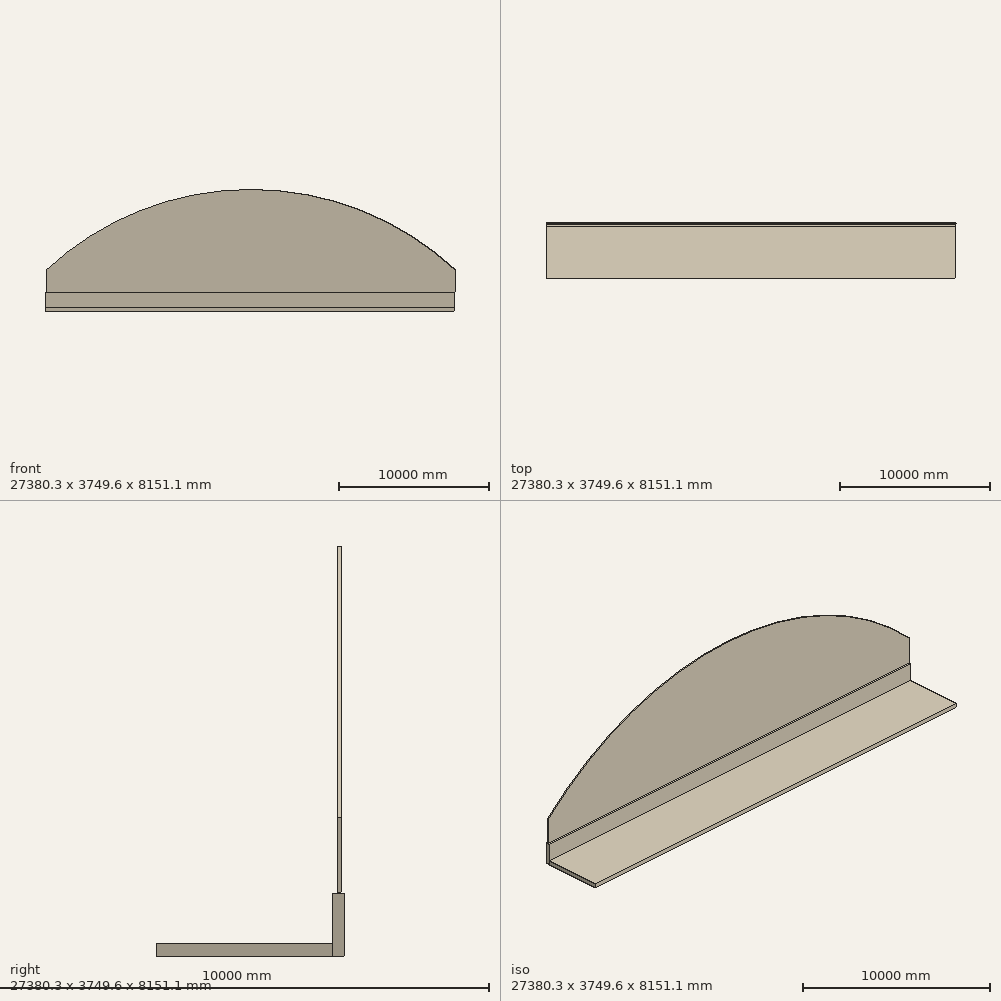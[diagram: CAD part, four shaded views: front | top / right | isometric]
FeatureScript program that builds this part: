
annotation { "Feature Type Name" : "Feature", "Feature Type Description" : "" }
export const myFeature = defineFeature(function(context is Context, id is Id, definition is map)
    precondition{}
    {
        {
            var Q0;
            Q0=qCreatedBy(makeId("Top.planeOp"),FACE);
            var sketch = newSketch(context, id + "F0", { "sketchPlane" : qUnion([Q0])});
            skLineSegment(sketch, "E0.bottom", {"start": v(-13653.67, -3086.65) * mm, "end": v(13646.33, -3086.65) * mm});
            skLineSegment(sketch, "E0.top", {"start": v(-13653.67, -6586.65) * mm, "end": v(13646.33, -6586.65) * mm});
            skLineSegment(sketch, "E0.left", {"start": v(-13653.67, -3086.65) * mm, "end": v(-13653.67, -6586.65) * mm});
            skLineSegment(sketch, "E0.right", {"start": v(13646.33, -3086.65) * mm, "end": v(13646.33, -6586.65) * mm});
            skSolve(sketch);
        }
        {
            var Q0;
            Q0=qCreatedBy(makeId("Top.planeOp"),FACE);
            var sketch = newSketch(context, id + "F1", { "sketchPlane" : qUnion([Q0])});
            skLineSegment(sketch, "E1.bottom", {"start": v(-13619.48, -3087.02) * mm, "end": v(13680.52, -3087.02) * mm});
            skLineSegment(sketch, "E1.top", {"start": v(-13619.48, -2837.02) * mm, "end": v(13680.52, -2837.02) * mm});
            skLineSegment(sketch, "E1.left", {"start": v(-13619.48, -3087.02) * mm, "end": v(-13619.48, -2837.02) * mm});
            skLineSegment(sketch, "E1.right", {"start": v(13680.52, -3087.02) * mm, "end": v(13680.52, -2837.02) * mm});
            skSolve(sketch);
        }
        {
            var Q0;
            Q0=qSketchRegion(id+"F0",true);
            extrude(context, id + "F2", {"entities" : qUnion([Q0]), "oppositeDirection" : true, "depth" : 250 * mm});
        }
        {
            var Q0;
            Q0=qSketchRegion(id+"F1",true);
            extrude(context, id + "F3", {"entities" : qUnion([Q0]), "depth" : 1000 * mm, "hasSecondDirection" : true, "secondDirectionOppositeDirection" : true, "secondDirectionDepth" : 250 * mm});
        }
        {
            var Q0;
            Q0=qCreatedBy(makeId("Front.planeOp"),FACE);
            var sketch = newSketch(context, id + "F4", { "sketchPlane" : qUnion([Q0])});
            skLineSegment(sketch, "E2.bottom", {"start": v(-13573.4, 1018.78) * mm, "end": v(13726.6, 1018.78) * mm});
            skLineSegment(sketch, "E2.left", {"start": v(-13573.4, 1018.78) * mm, "end": v(-13573.4, 2518.78) * mm});
            skLineSegment(sketch, "E2.right", {"start": v(13726.6, 1018.78) * mm, "end": v(13726.6, 2518.78) * mm});
            skArc(sketch, "E3", {"start": v(13726.6, 2518.78) * mm, "mid": v(76.6, 7901.06) * mm, "end": v(-13573.4, 2518.78) * mm});
            skSolve(sketch);
        }
        {
            var Q0;
            Q0=qSketchRegion(id+"F4",true);
            extrude(context, id + "F5", {"entities" : qUnion([Q0]), "depth" : 2975 * mm, "hasSecondDirection" : true, "secondDirectionOppositeDirection" : false, "secondDirectionDepth" : 2900 * mm});
        }
    });
